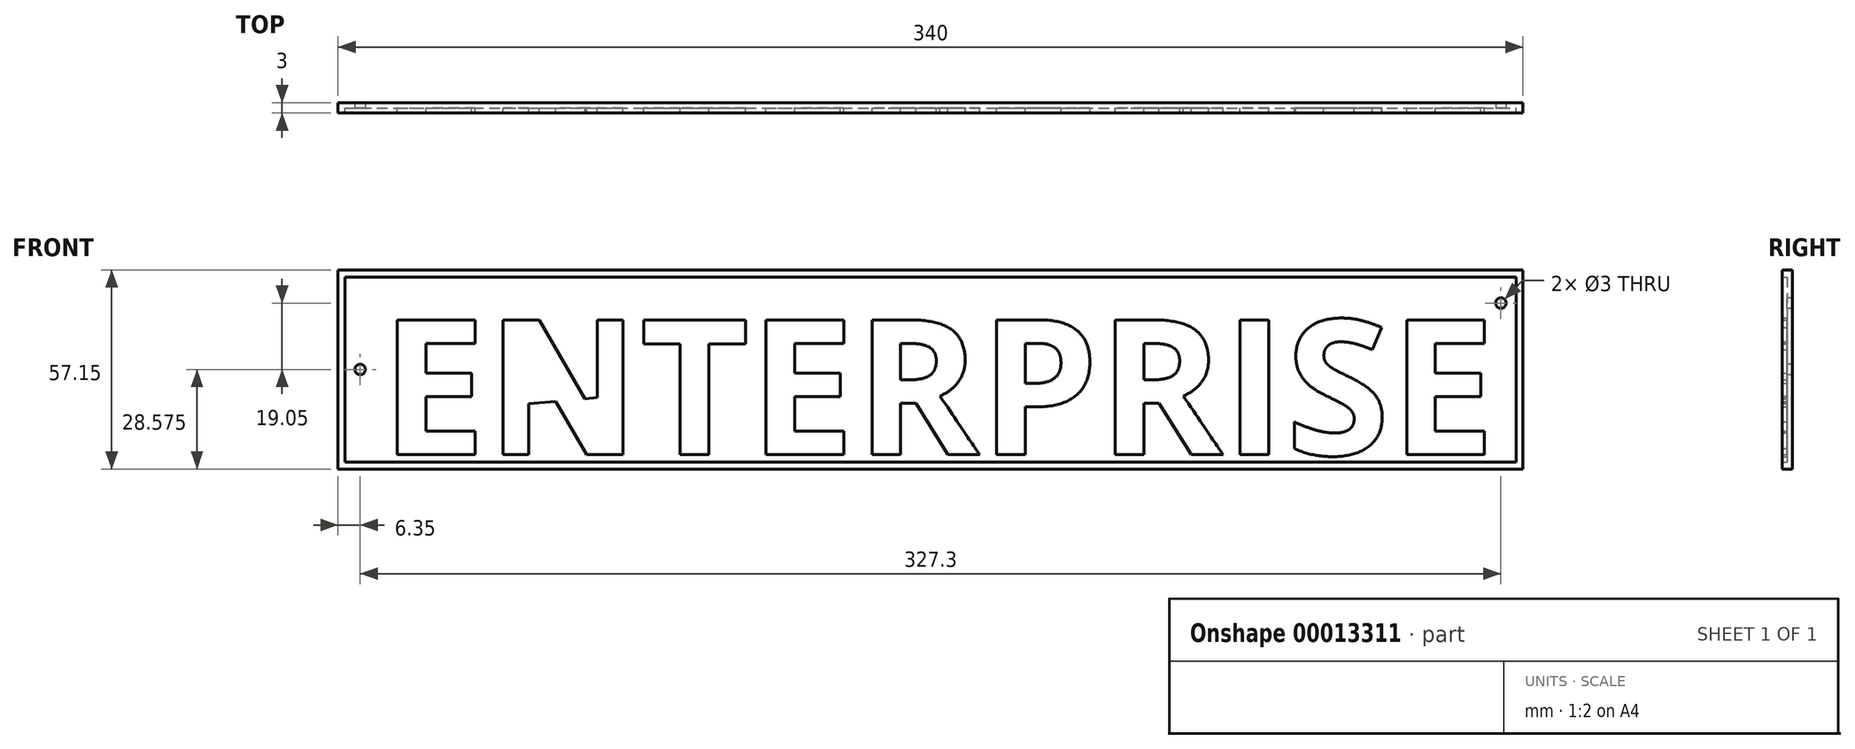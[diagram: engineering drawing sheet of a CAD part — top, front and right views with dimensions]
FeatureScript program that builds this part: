
annotation { "Feature Type Name" : "Feature", "Feature Type Description" : "" }
export const myFeature = defineFeature(function(context is Context, id is Id, definition is map)
    precondition{}
    {
        {
            var Q0;
            Q0=qCreatedBy(makeId("Front.planeOp"),FACE);
            var sketch = newSketch(context, id + "F0", { "sketchPlane" : qUnion([Q0])});
            skLineSegment(sketch, "E0.bottom", {"start": v(340, 57.15) * mm, "end": v(0, 57.15) * mm});
            skLineSegment(sketch, "E0.top", {"start": v(340, 0) * mm, "end": v(0, 0) * mm});
            skLineSegment(sketch, "E0.left", {"start": v(340, 57.15) * mm, "end": v(340, 0) * mm});
            skLineSegment(sketch, "E0.right", {"start": v(0, 57.15) * mm, "end": v(0, 0) * mm});
            skSolve(sketch);
        }
        {
            var Q0;
            Q0=qSketchRegion(id+"F0",true);
            extrude(context, id + "F1", {"entities" : qUnion([Q0]), "depth" : 1.5 * mm});
        }
        {
            var Q0;
            Q0=makeQuery(id+"F1.opExtrude","CAP_FACE",FACE,{"disambiguationData":[OSD([sQuery(id+"F0.wireOp",EDGE,"E0.bottom"),sQuery(id+"F0.wireOp",EDGE,"E0.top"),sQuery(id+"F0.wireOp",EDGE,"E0.left"),sQuery(id+"F0.wireOp",EDGE,"E0.right")])],"isStart":false});
            var sketch = newSketch(context, id + "F2", { "sketchPlane" : qUnion([Q0])});
            skLineSegment(sketch, "E1.bottom", {"start": v(0, 0) * mm, "end": v(340, 0) * mm});
            skLineSegment(sketch, "E1.top", {"start": v(0, 57.15) * mm, "end": v(340, 57.15) * mm});
            skLineSegment(sketch, "E1.left", {"start": v(0, 0) * mm, "end": v(0, 57.15) * mm});
            skLineSegment(sketch, "E1.right", {"start": v(340, 0) * mm, "end": v(340, 57.15) * mm});
            skLineSegment(sketch, "E2.bottom", {"start": v(2, 55.15) * mm, "end": v(338, 55.15) * mm});
            skLineSegment(sketch, "E2.top", {"start": v(2, 2) * mm, "end": v(338, 2) * mm});
            skLineSegment(sketch, "E2.left", {"start": v(2, 55.15) * mm, "end": v(2, 2) * mm});
            skLineSegment(sketch, "E2.right", {"start": v(338, 55.15) * mm, "end": v(338, 2) * mm});
            skSolve(sketch);
        }
        {
            var Q0;
            Q0=qSketchRegion(id+"F2",true);
            extrude(context, id + "F3", {"entities" : qUnion([Q0]), "operationType" : NewBodyOperationType.ADD, "depth" : 1.5 * mm});
        }
        {
            var Q0;
            Q0=makeQuery(id+"F1.opExtrude","CAP_FACE",FACE,{"disambiguationData":[OSD([sQuery(id+"F0.wireOp",EDGE,"E0.bottom"),sQuery(id+"F0.wireOp",EDGE,"E0.top"),sQuery(id+"F0.wireOp",EDGE,"E0.left"),sQuery(id+"F0.wireOp",EDGE,"E0.right")])],"isStart":false});
            var sketch = newSketch(context, id + "F4", { "sketchPlane" : qUnion([Q0])});
            skLineSegment(sketch, "E3.bottom", {"start": v(12.16, 14.95) * mm, "end": v(328.92, 43.14) * mm});
            skLineSegment(sketch, "E3.left", {"start": v(12.16, 14.95) * mm, "end": v(12.16, 4.1) * mm});
            skText(sketch, "E4", { "text": "ENTERPRISE", "fontName": "OpenSans-Bold.ttf"});
            const initialGuessF4  = {"E4": [0.01216, 0.0041, 1, 0, 0.03903]};
            skSetInitialGuess(sketch, initialGuessF4);
            skSolve(sketch);
        }
        {
            var Q0;
            Q0=qSketchRegion(id+"F4",true);
            extrude(context, id + "F5", {"entities" : qUnion([Q0]), "operationType" : NewBodyOperationType.ADD, "depth" : 1.5 * mm});
        }
        {
            var Q0;
            Q0=makeQuery(id+"F5.boolean.opBoolean","SPLIT",FACE,{"disambiguationData":[TD([makeQuery(id+"F3.opExtrude","SWEPT_FACE",FACE,{"disambiguationData":[OSD([sQuery(id+"F2.wireOp",EDGE,"E2.bottom")])]})])],"derivedFrom":makeQuery(id+"F1.opExtrude","CAP_FACE",FACE,{"disambiguationData":[OSD([sQuery(id+"F0.wireOp",EDGE,"E0.bottom"),sQuery(id+"F0.wireOp",EDGE,"E0.top"),sQuery(id+"F0.wireOp",EDGE,"E0.left"),sQuery(id+"F0.wireOp",EDGE,"E0.right")])],"isStart":false})});
            var sketch = newSketch(context, id + "F6", { "sketchPlane" : qUnion([Q0])});
            skCircle(sketch, "E5", {"center": v(6.35, 28.58) * mm, "radius": 1.5 * mm});
            skPoint(sketch, "E5.centerSnap0", {"position": v(2, 28.58) * mm});
            skCircle(sketch, "E6", {"center": v(333.65, 47.63) * mm, "radius": 1.5 * mm});
            skSolve(sketch);
        }
        {
            var Q0;
            Q0=qSketchRegion(id+"F6",true);
            extrude(context, id + "F7", {"entities" : qUnion([Q0]), "operationType" : NewBodyOperationType.REMOVE, "endBound" : BoundingType.THROUGH_ALL, "oppositeDirection" : true, "depth" : 25.4 * mm});
        }
    });
